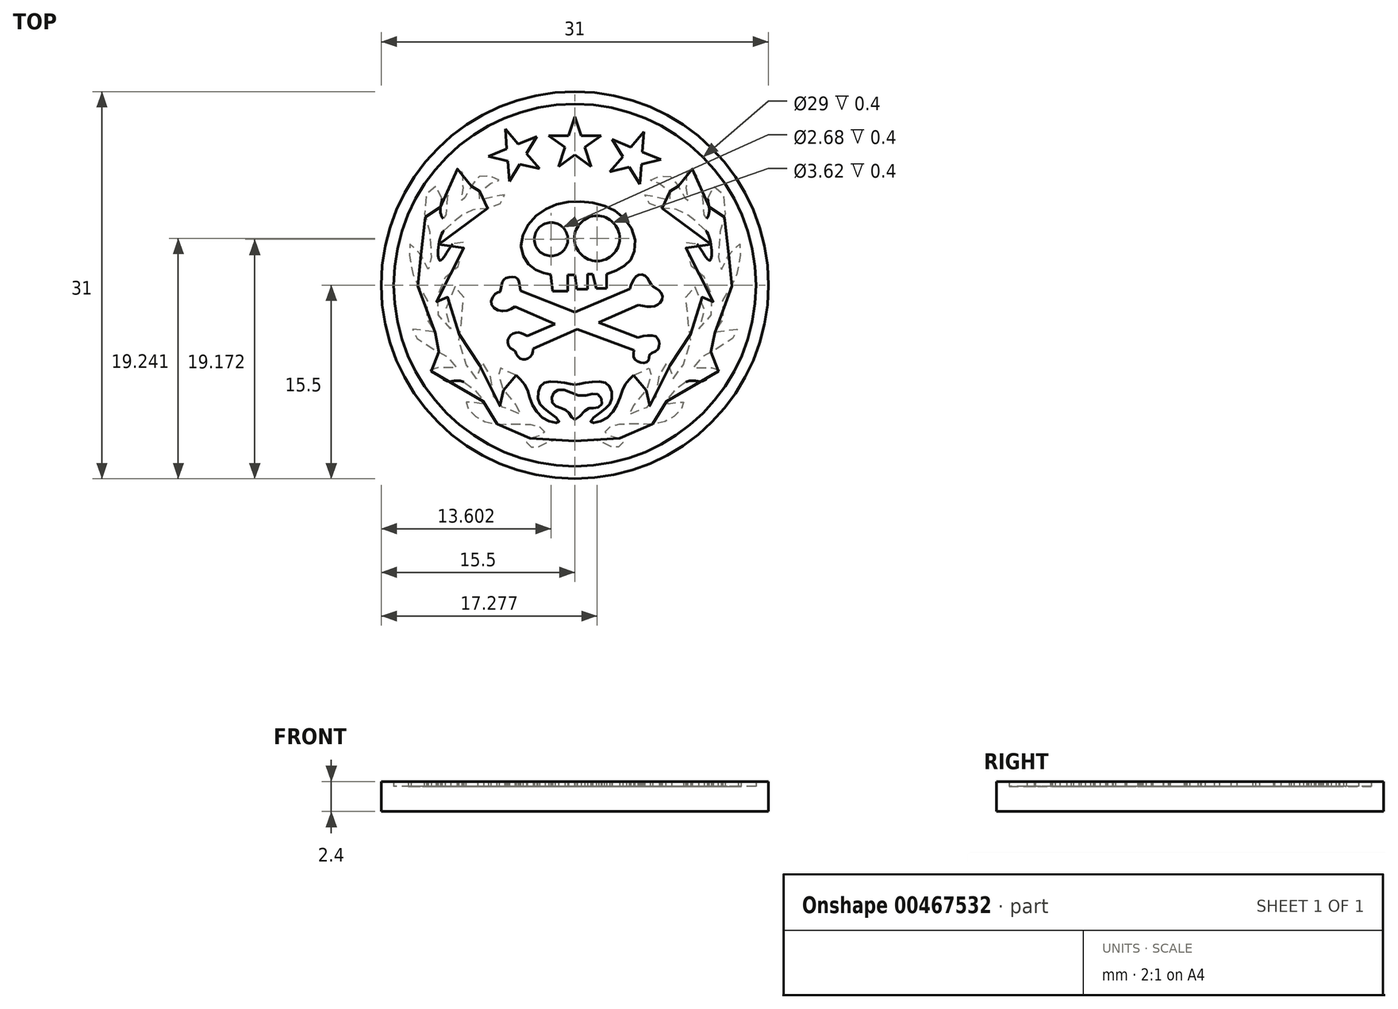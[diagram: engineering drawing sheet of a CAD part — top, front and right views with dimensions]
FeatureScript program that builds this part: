
annotation { "Feature Type Name" : "Feature", "Feature Type Description" : "" }
export const myFeature = defineFeature(function(context is Context, id is Id, definition is map)
    precondition{}
    {
        {
            var Q0;
            Q0=qCreatedBy(makeId("Top.planeOp"),FACE);
            var sketch = newSketch(context, id + "F0", { "sketchPlane" : qUnion([Q0])});
            skLineSegment(sketch, "E0", {"start": v(-26.65, 15) * mm, "end": v(26.65, -15) * mm, "construction": true});
            skCircle(sketch, "E1", {"center": v(0, 0) * mm, "radius": 15.5 * mm});
            skCircle(sketch, "E2", {"center": v(0, 0) * mm, "radius": 14.5 * mm});
            skLineSegment(sketch, "E3", {"start": v(-4.36, -0.44) * mm, "end": v(0, -2.17) * mm});
            skLineSegment(sketch, "E4", {"start": v(0, -2.17) * mm, "end": v(4.4, -0.3) * mm});
            skLineSegment(sketch, "E5", {"start": v(5.07, -1.6) * mm, "end": v(1.89, -2.98) * mm});
            skLineSegment(sketch, "E6", {"start": v(1.89, -2.98) * mm, "end": v(5.06, -4.21) * mm});
            skLineSegment(sketch, "E7", {"start": v(4.71, -5.2) * mm, "end": v(0.2, -3.54) * mm});
            skLineSegment(sketch, "E8", {"start": v(0.2, -3.54) * mm, "end": v(-3.33, -5.08) * mm});
            skLineSegment(sketch, "E9", {"start": v(-3.82, -4.08) * mm, "end": v(-1.58, -3.1) * mm});
            skLineSegment(sketch, "E10", {"start": v(-1.58, -3.1) * mm, "end": v(-4.8, -1.73) * mm});
            skFitSpline(sketch, "E11", {"points": [v(-4.8, -1.73) * mm, v(-5.69, -2.09) * mm, v(-6.58, -1.73) * mm, v(-6.62, -1.06) * mm, v(-6.18, -0.57) * mm, v(-6, -0.53) * mm, v(-5.87, 0) * mm, v(-5.69, 0.45) * mm, v(-5.33, 0.63) * mm, v(-4.8, 0.63) * mm, v(-4.53, 0.45) * mm, v(-4.36, -0.44) * mm], "startDerivative": vector(-7.12, -4.36) * mm, "endDerivative": vector(0.96, -9.3) * mm});
            skFitSpline(sketch, "E12", {"points": [v(4.4, -0.3) * mm, v(4.67, 0.4) * mm, v(5.11, 0.8) * mm, v(5.7, 0.72) * mm, v(6.14, 0) * mm, v(6.58, -0.3) * mm, v(7.03, -0.89) * mm, v(6.76, -1.46) * mm, v(6.14, -1.73) * mm, v(5.07, -1.6) * mm], "startDerivative": vector(1.89, 6.57) * mm, "endDerivative": vector(-8.28, 1.76) * mm});
            skFitSpline(sketch, "E13", {"points": [v(-3.82, -4.08) * mm, v(-4.36, -3.82) * mm, v(-4.8, -3.82) * mm, v(-5.2, -4.08) * mm, v(-5.38, -4.49) * mm, v(-5.2, -4.98) * mm, v(-4.8, -5.29) * mm, v(-4.62, -5.64) * mm, v(-4.18, -5.95) * mm, v(-3.82, -5.9) * mm, v(-3.47, -5.6) * mm, v(-3.33, -5.08) * mm], "startDerivative": vector(-5.41, 2.71) * mm, "endDerivative": vector(0.7, 5.77) * mm});
            skFitSpline(sketch, "E14", {"points": [v(4.71, -5.2) * mm, v(4.71, -5.78) * mm, v(5.07, -6.13) * mm, v(5.65, -6.22) * mm, v(5.92, -5.95) * mm, v(6, -5.55) * mm, v(6.58, -5.2) * mm, v(6.76, -4.75) * mm, v(6.72, -4.44) * mm, v(6.4, -4.08) * mm, v(5.47, -4.08) * mm, v(5.06, -4.21) * mm], "startDerivative": vector(-0.94, -6.42) * mm, "endDerivative": vector(-4.82, -2.22) * mm});
            skFitSpline(sketch, "E15", {"points": [v(-1.93, 0.84) * mm, v(-2.77, 1.06) * mm, v(-3.72, 1.7) * mm, v(-4.3, 3) * mm, v(-3.85, 4.66) * mm, v(-2.35, 6.09) * mm, v(-0.47, 6.67) * mm, v(1.75, 6.54) * mm, v(3.57, 5.69) * mm, v(4.76, 3.92) * mm, v(4.6, 2.28) * mm, v(3.84, 1.46) * mm, v(2.55, 0.87) * mm], "startDerivative": vector(-12.93, 3.14) * mm, "endDerivative": vector(-16.64, -5.48) * mm});
            skLineSegment(sketch, "E16", {"start": v(2.55, 0.87) * mm, "end": v(2.55, -0.25) * mm});
            skLineSegment(sketch, "E17", {"start": v(2.55, -0.25) * mm, "end": v(1.7, -0.25) * mm});
            skLineSegment(sketch, "E18", {"start": v(1.7, -0.25) * mm, "end": v(1.43, 0.87) * mm});
            skLineSegment(sketch, "E19", {"start": v(1.43, 0.87) * mm, "end": v(1.01, 0.87) * mm});
            skLineSegment(sketch, "E20", {"start": v(1.01, 0.87) * mm, "end": v(1.01, -0.31) * mm});
            skLineSegment(sketch, "E21", {"start": v(1.01, -0.31) * mm, "end": v(0.17, -0.31) * mm});
            skLineSegment(sketch, "E22", {"start": v(0.17, -0.31) * mm, "end": v(0, 0.82) * mm});
            skLineSegment(sketch, "E23", {"start": v(0, 0.82) * mm, "end": v(-0.58, 0.82) * mm});
            skLineSegment(sketch, "E24", {"start": v(-0.58, 0.82) * mm, "end": v(-0.58, -0.47) * mm});
            skLineSegment(sketch, "E25", {"start": v(-0.58, -0.47) * mm, "end": v(-1.8, -0.47) * mm});
            skLineSegment(sketch, "E26", {"start": v(-1.8, -0.47) * mm, "end": v(-1.93, 0.84) * mm});
            skCircle(sketch, "E27", {"center": v(-1.9, 3.67) * mm, "radius": 1.34 * mm});
            skCircle(sketch, "E28", {"center": v(1.78, 3.74) * mm, "radius": 1.81 * mm});
            skCircle(sketch, "E29.cCircle", {"center": v(0, 11.29) * mm, "radius": 2.21 * mm, "construction": true});
            skLineSegment(sketch, "E29.0", {"start": v(-1.3, 9.5) * mm, "end": v(-2.1, 11.97) * mm, "construction": true});
            skLineSegment(sketch, "E29.1", {"start": v(-2.1, 11.97) * mm, "end": v(0, 13.5) * mm, "construction": true});
            skLineSegment(sketch, "E29.2", {"start": v(0, 13.5) * mm, "end": v(2.1, 11.97) * mm, "construction": true});
            skLineSegment(sketch, "E29.3", {"start": v(2.1, 11.97) * mm, "end": v(1.3, 9.5) * mm});
            skLineSegment(sketch, "E29.4", {"start": v(1.3, 9.5) * mm, "end": v(-1.3, 9.5) * mm, "construction": true});
            skLineSegment(sketch, "E30", {"start": v(-2.1, 11.97) * mm, "end": v(-0.5, 11.97) * mm});
            skLineSegment(sketch, "E31", {"start": v(-0.5, 11.97) * mm, "end": v(0, 13.5) * mm});
            skLineSegment(sketch, "E32", {"start": v(0, 13.5) * mm, "end": v(0.5, 11.97) * mm});
            skLineSegment(sketch, "E33", {"start": v(0.5, 11.97) * mm, "end": v(2.1, 11.97) * mm});
            skLineSegment(sketch, "E34", {"start": v(2.1, 11.97) * mm, "end": v(0.8, 11.03) * mm});
            skLineSegment(sketch, "E35", {"start": v(0.8, 11.03) * mm, "end": v(1.3, 9.5) * mm});
            skLineSegment(sketch, "E36", {"start": v(1.3, 9.5) * mm, "end": v(0, 10.44) * mm});
            skLineSegment(sketch, "E37", {"start": v(0, 10.44) * mm, "end": v(-1.3, 9.5) * mm});
            skLineSegment(sketch, "E38", {"start": v(-1.3, 9.5) * mm, "end": v(-0.8, 11.03) * mm});
            skLineSegment(sketch, "E39", {"start": v(-0.8, 11.03) * mm, "end": v(-2.1, 11.97) * mm});
            skLineSegment(sketch, "E40.1.0", {"start": v(-5.45, 10.91) * mm, "end": v(-5.57, 12.51) * mm});
            skLineSegment(sketch, "E40.1.1", {"start": v(-5.57, 12.51) * mm, "end": v(-4.53, 11.3) * mm});
            skLineSegment(sketch, "E40.1.2", {"start": v(-4.53, 11.3) * mm, "end": v(-3.04, 11.9) * mm});
            skLineSegment(sketch, "E40.1.3", {"start": v(-3.04, 11.9) * mm, "end": v(-3.88, 10.54) * mm});
            skLineSegment(sketch, "E40.1.4", {"start": v(-3.88, 10.54) * mm, "end": v(-2.84, 9.32) * mm});
            skLineSegment(sketch, "E40.1.5", {"start": v(-2.84, 9.32) * mm, "end": v(-4.4, 9.7) * mm});
            skLineSegment(sketch, "E40.1.6", {"start": v(-4.4, 9.7) * mm, "end": v(-5.24, 8.32) * mm});
            skLineSegment(sketch, "E40.1.7", {"start": v(-5.24, 8.32) * mm, "end": v(-5.37, 9.92) * mm});
            skLineSegment(sketch, "E40.1.8", {"start": v(-5.37, 9.92) * mm, "end": v(-6.93, 10.3) * mm});
            skLineSegment(sketch, "E40.1.9", {"start": v(-6.93, 10.3) * mm, "end": v(-5.45, 10.91) * mm});
            skPoint(sketch, "E40.center", {"position": v(-0.3, -1) * mm});
            skLineSegment(sketch, "E40.anchor1", {"start": v(-0.3, -1) * mm, "end": v(-1.3, 9.5) * mm, "construction": true});
            skLineSegment(sketch, "E40.anchor2", {"start": v(-0.3, -1) * mm, "end": v(-5.24, 8.32) * mm, "construction": true});
            skLineSegment(sketch, "E41.1.0", {"start": v(3, 11.67) * mm, "end": v(4.48, 11.05) * mm});
            skLineSegment(sketch, "E41.1.1", {"start": v(4.48, 11.05) * mm, "end": v(5.52, 12.27) * mm});
            skLineSegment(sketch, "E41.1.2", {"start": v(5.52, 12.27) * mm, "end": v(5.4, 10.67) * mm});
            skLineSegment(sketch, "E41.1.3", {"start": v(5.4, 10.67) * mm, "end": v(6.88, 10.06) * mm});
            skLineSegment(sketch, "E41.1.4", {"start": v(6.88, 10.06) * mm, "end": v(5.32, 9.68) * mm});
            skLineSegment(sketch, "E41.1.5", {"start": v(5.32, 9.68) * mm, "end": v(5.2, 8.08) * mm});
            skLineSegment(sketch, "E41.1.6", {"start": v(5.2, 8.08) * mm, "end": v(4.35, 9.45) * mm});
            skLineSegment(sketch, "E41.1.7", {"start": v(4.35, 9.45) * mm, "end": v(2.8, 9.07) * mm});
            skLineSegment(sketch, "E41.1.8", {"start": v(2.8, 9.07) * mm, "end": v(3.84, 10.3) * mm});
            skLineSegment(sketch, "E41.1.9", {"start": v(3.84, 10.3) * mm, "end": v(3, 11.67) * mm});
            skPoint(sketch, "E41.center", {"position": v(-0.32, -1) * mm});
            skLineSegment(sketch, "E41.anchor1", {"start": v(-0.32, -1) * mm, "end": v(-1.3, 9.5) * mm, "construction": true});
            skLineSegment(sketch, "E41.anchor2", {"start": v(-0.32, -1) * mm, "end": v(2.8, 9.07) * mm, "construction": true});
            skFitSpline(sketch, "E42", {"points": [v(0, -10.78) * mm, v(-0.43, -10.28) * mm, v(-0.85, -9.94) * mm, v(-1.73, -9.52) * mm, v(-1.78, -8.77) * mm, v(-1.1, -8.35) * mm, v(0.53, -8.85) * mm, v(1.79, -8.73) * mm, v(2.17, -9.48) * mm, v(1.58, -9.86) * mm, v(1, -9.9) * mm, v(0, -10.78) * mm]});
            skFitSpline(sketch, "E43", {"points": [v(4.7, -7.23) * mm, v(5.9, -6.66) * mm, v(6.25, -6.77) * mm, v(6.1, -7.23) * mm, v(5.9, -8.03) * mm, v(5.05, -9.27) * mm, v(4.17, -10.36) * mm, v(5.22, -9.97) * mm, v(6.25, -9.48) * mm, v(6.6, -8.39) * mm, v(7.02, -6.48) * mm, v(7.52, -6.2) * mm, v(7.94, -7.58) * mm, v(9, -5.53) * mm, v(9.28, -3.94) * mm, v(8.9, -1.8) * mm, v(9.31, 0) * mm, v(10.37, -1.86) * mm, v(9.95, -3.49) * mm, v(10.94, -2.4) * mm, v(10.9, -0.63) * mm, v(10.27, 0.74) * mm, v(9.31, 1.52) * mm, v(9, 3.67) * mm, v(9.7, 3.39) * mm, v(10.8, 1.98) * mm, v(10.76, 3.85) * mm, v(9.74, 5.05) * mm, v(8.26, 6.03) * mm, v(6.1, 6.42) * mm, v(5.68, 7.27) * mm, v(7.66, 6.8) * mm, v(7.3, 7.87) * mm, v(6.07, 8.4) * mm, v(7.23, 8.78) * mm, v(8.15, 8.15) * mm, v(9.03, 6.7) * mm, v(8.93, 7.9) * mm, v(9.2, 9.38) * mm, v(10.13, 7.62) * mm, v(10.44, 5.26) * mm, v(10.76, 5.9) * mm, v(10.65, 7.23) * mm, v(11.36, 7.97) * mm, v(12.06, 6.21) * mm, v(11.57, 3.99) * mm, v(11.68, 1.24) * mm, v(12.35, 2.47) * mm, v(13.26, 3.28) * mm, v(13.16, 1.9) * mm, v(12.63, 0) * mm, v(11.85, -1.05) * mm, v(11.75, -3.1) * mm, v(11.08, -3.84) * mm, v(12.24, -3.56) * mm, v(13.12, -3.66) * mm, v(11.6, -4.97) * mm, v(10.2, -5.74) * mm, v(9.5, -6.66) * mm, v(11.7, -6.59) * mm, v(11, -7.23) * mm, v(10.02, -7.72) * mm, v(8.9, -7.75) * mm, v(7.34, -9.48) * mm, v(8.64, -9.34) * mm, v(7.97, -10.5) * mm, v(5.65, -11.14) * mm, v(2.9, -11.31) * mm, v(2.44, -11.88) * mm, v(3.85, -12.44) * mm, v(3.36, -13) * mm, v(1.95, -12.48) * mm, v(0, -12.48) * mm], "startDerivative": vector(98.37, 59.23) * mm, "endDerivative": vector(-116.14, -18.96) * mm});
            skFitSpline(sketch, "E44", {"points": [v(4.7, -7.23) * mm, v(3.96, -8.06) * mm, v(3.39, -9.57) * mm, v(2.15, -10.87) * mm, v(1.27, -10.95) * mm, v(1.98, -10.22) * mm, v(2.87, -9.4) * mm, v(2.84, -8.25) * mm, v(2.2, -7.75) * mm, v(0.75, -7.83) * mm, v(0, -7.98) * mm], "startDerivative": vector(-8.45, -7.47) * mm, "endDerivative": vector(-8.1, -1.7) * mm});
            skFitSpline(sketch, "E45.MirrorCS", {"points": [v(-4.7, -7.23) * mm, v(-3.96, -8.06) * mm, v(-3.39, -9.57) * mm, v(-2.15, -10.87) * mm, v(-1.27, -10.95) * mm, v(-1.98, -10.22) * mm, v(-2.87, -9.4) * mm, v(-2.84, -8.25) * mm, v(-2.2, -7.75) * mm, v(-0.75, -7.83) * mm, v(0, -7.98) * mm], "startDerivative": vector(8.45, -7.47) * mm, "endDerivative": vector(8.1, -1.7) * mm});
            skFitSpline(sketch, "E46.MirrorCS", {"points": [v(-4.7, -7.23) * mm, v(-5.9, -6.66) * mm, v(-6.25, -6.77) * mm, v(-6.1, -7.23) * mm, v(-5.9, -8.03) * mm, v(-5.05, -9.27) * mm, v(-4.17, -10.36) * mm, v(-5.22, -9.97) * mm, v(-6.25, -9.48) * mm, v(-6.6, -8.39) * mm, v(-7.02, -6.48) * mm, v(-7.52, -6.2) * mm, v(-7.94, -7.58) * mm, v(-9, -5.53) * mm, v(-9.28, -3.94) * mm, v(-8.9, -1.8) * mm, v(-9.31, 0) * mm, v(-10.37, -1.86) * mm, v(-9.95, -3.49) * mm, v(-10.94, -2.4) * mm, v(-10.9, -0.63) * mm, v(-10.27, 0.74) * mm, v(-9.31, 1.52) * mm, v(-9, 3.67) * mm, v(-9.7, 3.39) * mm, v(-10.8, 1.98) * mm, v(-10.76, 3.85) * mm, v(-9.74, 5.05) * mm, v(-8.26, 6.03) * mm, v(-6.1, 6.42) * mm, v(-5.68, 7.27) * mm, v(-7.66, 6.8) * mm, v(-7.3, 7.87) * mm, v(-6.07, 8.4) * mm, v(-7.23, 8.78) * mm, v(-8.15, 8.15) * mm, v(-9.03, 6.7) * mm, v(-8.93, 7.9) * mm, v(-9.2, 9.38) * mm, v(-10.13, 7.62) * mm, v(-10.44, 5.26) * mm, v(-10.76, 5.9) * mm, v(-10.65, 7.23) * mm, v(-11.36, 7.97) * mm, v(-12.06, 6.21) * mm, v(-11.57, 3.99) * mm, v(-11.68, 1.24) * mm, v(-12.35, 2.47) * mm, v(-13.26, 3.28) * mm, v(-13.16, 1.9) * mm, v(-12.63, 0) * mm, v(-11.85, -1.05) * mm, v(-11.75, -3.1) * mm, v(-11.08, -3.84) * mm, v(-12.24, -3.56) * mm, v(-13.12, -3.66) * mm, v(-11.6, -4.97) * mm, v(-10.2, -5.74) * mm, v(-9.5, -6.66) * mm, v(-11.7, -6.59) * mm, v(-11, -7.23) * mm, v(-10.02, -7.72) * mm, v(-8.9, -7.75) * mm, v(-7.34, -9.48) * mm, v(-8.64, -9.34) * mm, v(-7.97, -10.5) * mm, v(-5.65, -11.14) * mm, v(-2.9, -11.31) * mm, v(-2.44, -11.88) * mm, v(-3.85, -12.44) * mm, v(-3.36, -13) * mm, v(-1.95, -12.48) * mm, v(0, -12.48) * mm], "startDerivative": vector(-98.37, 59.23) * mm, "endDerivative": vector(116.14, -18.96) * mm});
            skSolve(sketch);
        }
        {
            var Q0;
            Q0=qCreatedBy(makeId("Top.planeOp"),FACE);
            var sketch = newSketch(context, id + "F1", { "sketchPlane" : qUnion([Q0])});
            skCircle(sketch, "E47", {"center": v(0, 0) * mm, "radius": 15.5 * mm});
            skSolve(sketch);
        }
        {
            var Q0;
            Q0 = qSketchRegion(id + "F1", true);
            extrude(context, id + "F2", {"entities" : qUnion([Q0]), "depth" : 2 * mm});
        }
        {
            var Q0;
            Q0 = qSketchRegion(id + "F0", true);
            extrude(context, id + "F3", {"entities" : qUnion([Q0]), "operationType" : NewBodyOperationType.ADD, "depth" : 2.4 * mm});
        }
        {
            var Q0;
            Q0=makeQuery(id+"F0.imprint","IMPRINT",FACE,{"disambiguationData":[TD([[makeQuery(id+"F0.imprint","IMPRINT",EDGE,{"derivedFrom":sQuery(id+"F0.wireOp",EDGE,"E3")}),-1.0]])]});
            var Q1;
            Q1=makeQuery(id+"F0.imprint","IMPRINT",FACE,{"disambiguationData":[TD([[makeQuery(id+"F0.imprint","IMPRINT",EDGE,{"derivedFrom":sQuery(id+"F0.wireOp",EDGE,"E15")}),-1.0]])]});
            var Q2;
            Q2=makeQuery(id+"F0.imprint","IMPRINT",FACE,{"disambiguationData":[TD([[makeQuery(id+"F0.imprint","IMPRINT",EDGE,{"derivedFrom":sQuery(id+"F0.wireOp",EDGE,"E40.1.0")}),-1.0]])]});
            var Q3;
            Q3=makeQuery(id+"F0.imprint","IMPRINT",FACE,{"disambiguationData":[TD([[makeQuery(id+"F0.imprint","IMPRINT",EDGE,{"derivedFrom":sQuery(id+"F0.wireOp",EDGE,"E30")}),-1.0]])]});
            var Q4;
            Q4=makeQuery(id+"F0.imprint","IMPRINT",FACE,{"disambiguationData":[TD([[makeQuery(id+"F0.imprint","IMPRINT",EDGE,{"derivedFrom":sQuery(id+"F0.wireOp",EDGE,"E41.1.0")}),-1.0]])]});
            var Q5;
            Q5=makeQuery(id+"F0.imprint","IMPRINT",FACE,{"disambiguationData":[TD([[makeQuery(id+"F0.imprint","IMPRINT",EDGE,{"derivedFrom":sQuery(id+"F0.wireOp",EDGE,"E42")}),1.0]])]});
            extrude(context, id + "F4", {"entities" : qUnion([Q0, Q1, Q2, Q3, Q4, Q5]), "operationType" : NewBodyOperationType.ADD, "depth" : 2.4 * mm});
        }
    });
